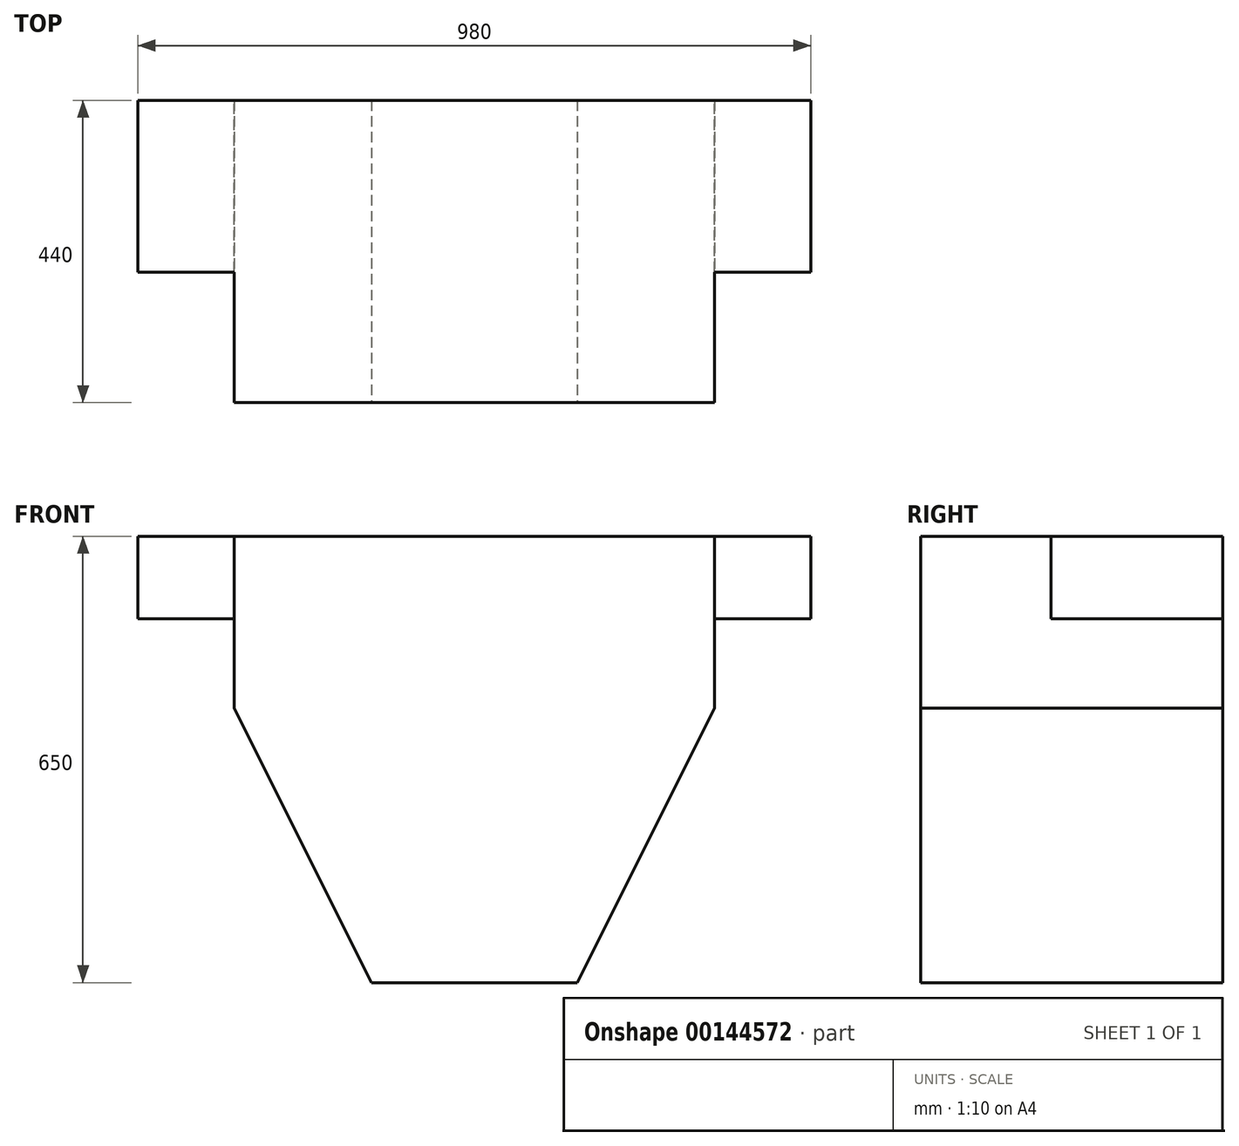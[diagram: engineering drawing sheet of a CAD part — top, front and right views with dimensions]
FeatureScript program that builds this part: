
annotation { "Feature Type Name" : "Feature", "Feature Type Description" : "" }
export const myFeature = defineFeature(function(context is Context, id is Id, definition is map)
    precondition{}
    {
        {
            var Q0;
            Q0=qCreatedBy(makeId("Top.planeOp"),FACE);
            var sketch = newSketch(context, id + "F0", { "sketchPlane" : qUnion([Q0])});
            skLineSegment(sketch, "E0.bottom", {"start": v(490, -220) * mm, "end": v(-490, -220) * mm});
            skLineSegment(sketch, "E0.top", {"start": v(490, 220) * mm, "end": v(-490, 220) * mm});
            skLineSegment(sketch, "E0.left", {"start": v(490, -220) * mm, "end": v(490, 220) * mm});
            skLineSegment(sketch, "E0.right", {"start": v(-490, -220) * mm, "end": v(-490, 220) * mm});
            skPoint(sketch, "E0.middle", {"position": v(0, 0) * mm});
            skSolve(sketch);
        }
        {
            var Q0;
            Q0 = qSketchRegion(id + "F0", true);
            extrude(context, id + "F1", {"entities" : qUnion([Q0]), "depth" : 650 * mm});
        }
        {
            var Q0;
            Q0=makeQuery(id+"F1.opExtrude","SWEPT_FACE",FACE,{"disambiguationData":[OSD([sQuery(id+"F0.wireOp",EDGE,"E0.bottom")])]});
            var sketch = newSketch(context, id + "F2", { "sketchPlane" : qUnion([Q0])});
            skLineSegment(sketch, "E1.bottom", {"start": v(-490, 650) * mm, "end": v(-350, 650) * mm});
            skLineSegment(sketch, "E1.top", {"start": v(-490, 0) * mm, "end": v(-350, 0) * mm});
            skLineSegment(sketch, "E1.left", {"start": v(-490, 650) * mm, "end": v(-490, 0) * mm});
            skLineSegment(sketch, "E1.right", {"start": v(-350, 650) * mm, "end": v(-350, 0) * mm});
            skLineSegment(sketch, "E2.bottom", {"start": v(490, 650) * mm, "end": v(350, 650) * mm});
            skLineSegment(sketch, "E2.top", {"start": v(490, 0) * mm, "end": v(350, 0) * mm});
            skLineSegment(sketch, "E2.left", {"start": v(490, 650) * mm, "end": v(490, 0) * mm});
            skLineSegment(sketch, "E2.right", {"start": v(350, 650) * mm, "end": v(350, 0) * mm});
            skSolve(sketch);
        }
        {
            var Q0;
            Q0 = qSketchRegion(id + "F2", true);
            extrude(context, id + "F3", {"entities" : qUnion([Q0]), "operationType" : NewBodyOperationType.REMOVE, "oppositeDirection" : true, "depth" : 190 * mm});
        }
        {
            var Q0;
            Q0=makeQuery(id+"F1.opExtrude","SWEPT_FACE",FACE,{"disambiguationData":[OSD([sQuery(id+"F0.wireOp",EDGE,"E0.top")])]});
            var sketch = newSketch(context, id + "F4", { "sketchPlane" : qUnion([Q0])});
            skLineSegment(sketch, "E3.bottom", {"start": v(-490, 0) * mm, "end": v(-350, 0) * mm});
            skLineSegment(sketch, "E3.top", {"start": v(-490, 530) * mm, "end": v(-350, 530) * mm});
            skLineSegment(sketch, "E3.left", {"start": v(-490, 0) * mm, "end": v(-490, 530) * mm});
            skLineSegment(sketch, "E3.right", {"start": v(-350, 0) * mm, "end": v(-350, 530) * mm});
            skLineSegment(sketch, "E4.bottom", {"start": v(490, 0) * mm, "end": v(350, 0) * mm});
            skLineSegment(sketch, "E4.top", {"start": v(490, 530) * mm, "end": v(350, 530) * mm});
            skLineSegment(sketch, "E4.left", {"start": v(490, 0) * mm, "end": v(490, 530) * mm});
            skLineSegment(sketch, "E4.right", {"start": v(350, 0) * mm, "end": v(350, 530) * mm});
            skSolve(sketch);
        }
        {
            var Q0;
            Q0 = qSketchRegion(id + "F4", true);
            extrude(context, id + "F5", {"entities" : qUnion([Q0]), "operationType" : NewBodyOperationType.REMOVE, "endBound" : BoundingType.THROUGH_ALL, "oppositeDirection" : true, "depth" : 25 * mm});
        }
        {
            var Q0;
            Q0=makeQuery(id+"F1.opExtrude","SWEPT_FACE",FACE,{"disambiguationData":[OSD([sQuery(id+"F0.wireOp",EDGE,"E0.bottom")])]});
            var sketch = newSketch(context, id + "F6", { "sketchPlane" : qUnion([Q0])});
            skLineSegment(sketch, "E5", {"start": v(-350, 0) * mm, "end": v(-150, 0) * mm});
            skLineSegment(sketch, "E6", {"start": v(-150, 0) * mm, "end": v(-350, 400) * mm});
            skLineSegment(sketch, "E7", {"start": v(-350, 400) * mm, "end": v(-350, 0) * mm});
            skLineSegment(sketch, "E8", {"start": v(150, 0) * mm, "end": v(350, 400) * mm});
            skLineSegment(sketch, "E9", {"start": v(350, 400) * mm, "end": v(350, 0) * mm});
            skLineSegment(sketch, "E10", {"start": v(350, 0) * mm, "end": v(150, 0) * mm});
            skSolve(sketch);
        }
        {
            var Q0;
            Q0 = qSketchRegion(id + "F6", true);
            extrude(context, id + "F7", {"entities" : qUnion([Q0]), "operationType" : NewBodyOperationType.REMOVE, "endBound" : BoundingType.THROUGH_ALL, "oppositeDirection" : true, "depth" : 25 * mm});
        }
    });
